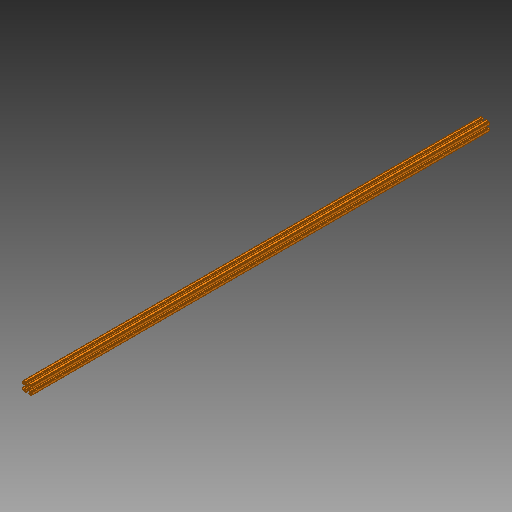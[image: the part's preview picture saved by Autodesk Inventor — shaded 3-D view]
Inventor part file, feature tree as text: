
AUTODESK INVENTOR PART (.ipt)
format: ipt  version: 2017 SP1 (Build 210196100, 196)  size: 231,936 bytes
history: native  units: in
note: dims shown in document units (in); Inventor stores cm internally (conversion verified against a paired STEP export)
features: extrude x1, pattern_circular x1, sketch x1
ambient origin geometry x8: Origin, YZ Plane, XZ Plane, XY Plane, X Axis, Y Axis, Z Axis, Center Point
bodies: Solid1 (feature_tree)
feature tree (3):
  extrude  "Extrusion1"  TaperAngle=45.0deg  [1 undecoded]
  pattern_circular  "Circular Pattern1"  [2 undecoded]
  sketch  "Sketch1"  dims[d0=0.16in d1=45.0deg d10=0.0312in d13=0.1015in d14=0.069in d21=0.061in d23=0.01in d24=0.115in d25=48.0in d26=0.0in d27=1.5748in d28=360.0deg d30=0.5in d32=0.375in d33=0.1875in d34=0.06in]
note: 3 required parameter values undecoded (feature->parameter linkage not recoverable at this tier; creation-order binding heuristic only, values carry confidence <= 0.55)
